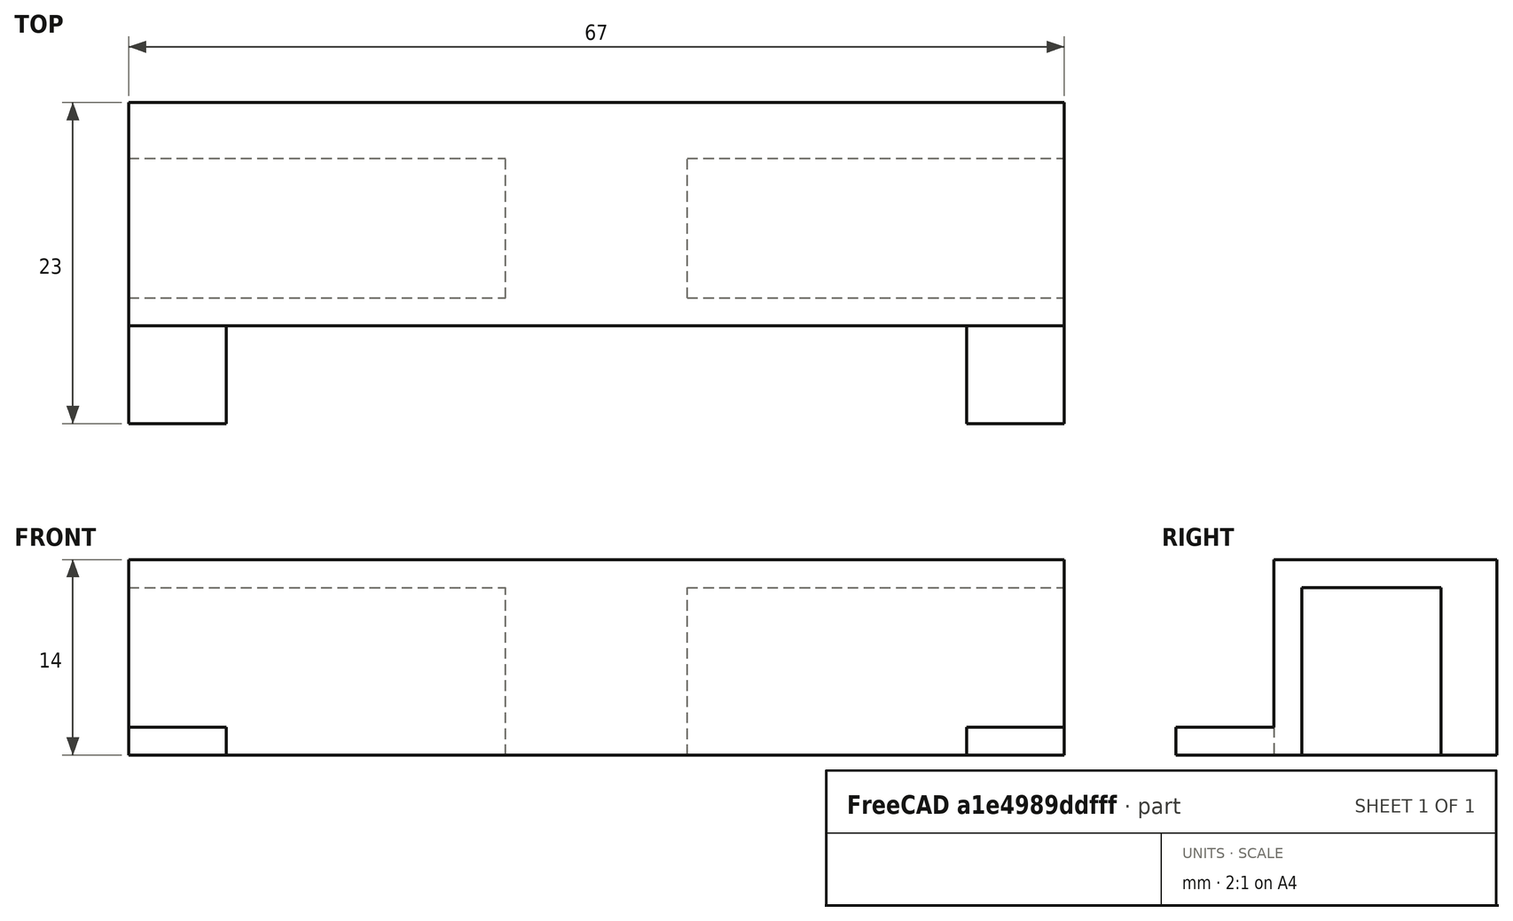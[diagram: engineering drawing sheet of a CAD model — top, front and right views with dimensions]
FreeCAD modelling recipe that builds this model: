
FCSTD DOCUMENT  (FreeCAD 0.16R6706 (Git))
Label: Sujeta Motores
License: All rights reserved
LicenseURL: http://en.wikipedia.org/wiki/All_rights_reserved
objects: Part::Box×5, Part::Cut×2, Part::MultiFuse×2
note: 9 computed .brp shape members not serialized (recipe doc carries the construction recipe); baked Part::Feature solids carry a one-line shape summary decoded from their .brp

FEATURE [Part::Box] Box  label="Cubo"
  Height = 14
  Length = 67
  Width = 16
FEATURE [Part::Box] Box001  label="Cubo001"
  Height = 12
  Length = 27
  Placement = pos=(0,2,0) rot=(0,0,1;0rad)
  Width = 10
FEATURE [Part::Box] Box002  label="Cubo002"
  Height = 12
  Length = 27
  Placement = pos=(40,2,0) rot=(0,0,1;0rad)
  Width = 10
FEATURE [Part::Cut] Cut
  Base = -> Box
  Tool = -> Box001
FEATURE [Part::Cut] Cut001  label="Pieza1"
  Base = -> Cut
  Tool = -> Box002
FEATURE [Part::Box] Box003  label="Cubo003"
  Height = 2
  Length = 7
  Placement = pos=(0,-7,0) rot=(0,0,1;0rad)
  Width = 9
FEATURE [Part::Box] Box004  label="Cubo004"
  Height = 2
  Length = 7
  Placement = pos=(60,-7,0) rot=(0,0,1;0rad)
  Width = 9
FEATURE [Part::MultiFuse] Fusion
  Shapes = -> [Box004,Box003]
FEATURE [Part::MultiFuse] Fusion001
  Shapes = -> [Cut001,Fusion]
